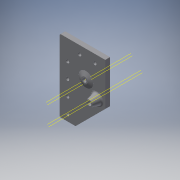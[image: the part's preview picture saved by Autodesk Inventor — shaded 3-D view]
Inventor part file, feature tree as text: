
AUTODESK INVENTOR PART (.ipt)
format: ipt  version: 2018 (Build 220112000, 112)  size: 217,088 bytes
history: native  units: in
note: dims shown in document units (in); Inventor stores cm internally (conversion verified against a paired STEP export)
features: sketch x8, extrude x6, plane x4, revolve x2, fillet x2, projected_geometry x2
ambient origin geometry x8: Origin, YZ Plane, XZ Plane, XY Plane, X Axis, Y Axis, Z Axis, Center Point
bodies: Solid1 (feature_tree)
feature tree (24):
  extrude  "Extrusion1"  Depth=0.7874in
  extrude  "Extrusion2"  Depth=3.5433in
  plane  "Work Plane2"
  revolve  "Revolution1"  [1 undecoded]
  extrude  "Extrusion3"  Depth=0.5512in
  extrude  "Extrusion4"  [1 undecoded]
  extrude  "Extrusion5"  Depth=0.0787in
  plane  "Work Plane4"
  revolve  "Revolution2"  [1 undecoded]
  fillet  "Fillet2"  Radius=0.1575in
  fillet  "Fillet3"  Radius=0.1654in
  extrude  "Extrusion6"  Depth=0.3937in
  sketch  "Sketch1"  dims[d0=0.7874in d1=0.7874in]
  sketch  "Sketch2"  dims[d2=3.5433in d3=3.5433in]
  plane  "Work Plane1"
  sketch  "Sketch3"  dims[d4=0.2362in d5=0.0in d6=0.1969in]
  sketch  "Sketch4"  dims[d7=1.2992in d8=0.5512in]
  projected_geometry  "Projected Loop1"
  sketch  "Sketch5"  dims[d9=0.2362in d10=0.0in d11=-0.0984in]
  sketch  "Sketch7"  dims[d12=0.3543in d13=0.0787in]
  plane  "Work Plane3"
  sketch  "Sketch8"  dims[d14=90.0deg d15=0.2362in d16=0.0in d17=0.1575in d18=0.1654in]
  projected_geometry  "Projected Loop2"
  sketch  "Sketch9"  dims[d19=0.315in d20=0.748in d21=0.748in d22=0.748in d23=0.315in d24=0.748in d25=0.748in d26=0.748in d27=0.2362in d28=0.0in d30=0.3543in d32=0.3543in d33=0.1969in d34=0.0in d35=0.0984in d36=0.1575in d37=0.0591in d38=0.3937in d39=90.0deg d40=0.0787in d41=0.0787in d42=1.2992in d43=0.3937in d44=0.0in]
note: 3 required parameter values undecoded (feature->parameter linkage not recoverable at this tier; creation-order binding heuristic only, values carry confidence <= 0.55)